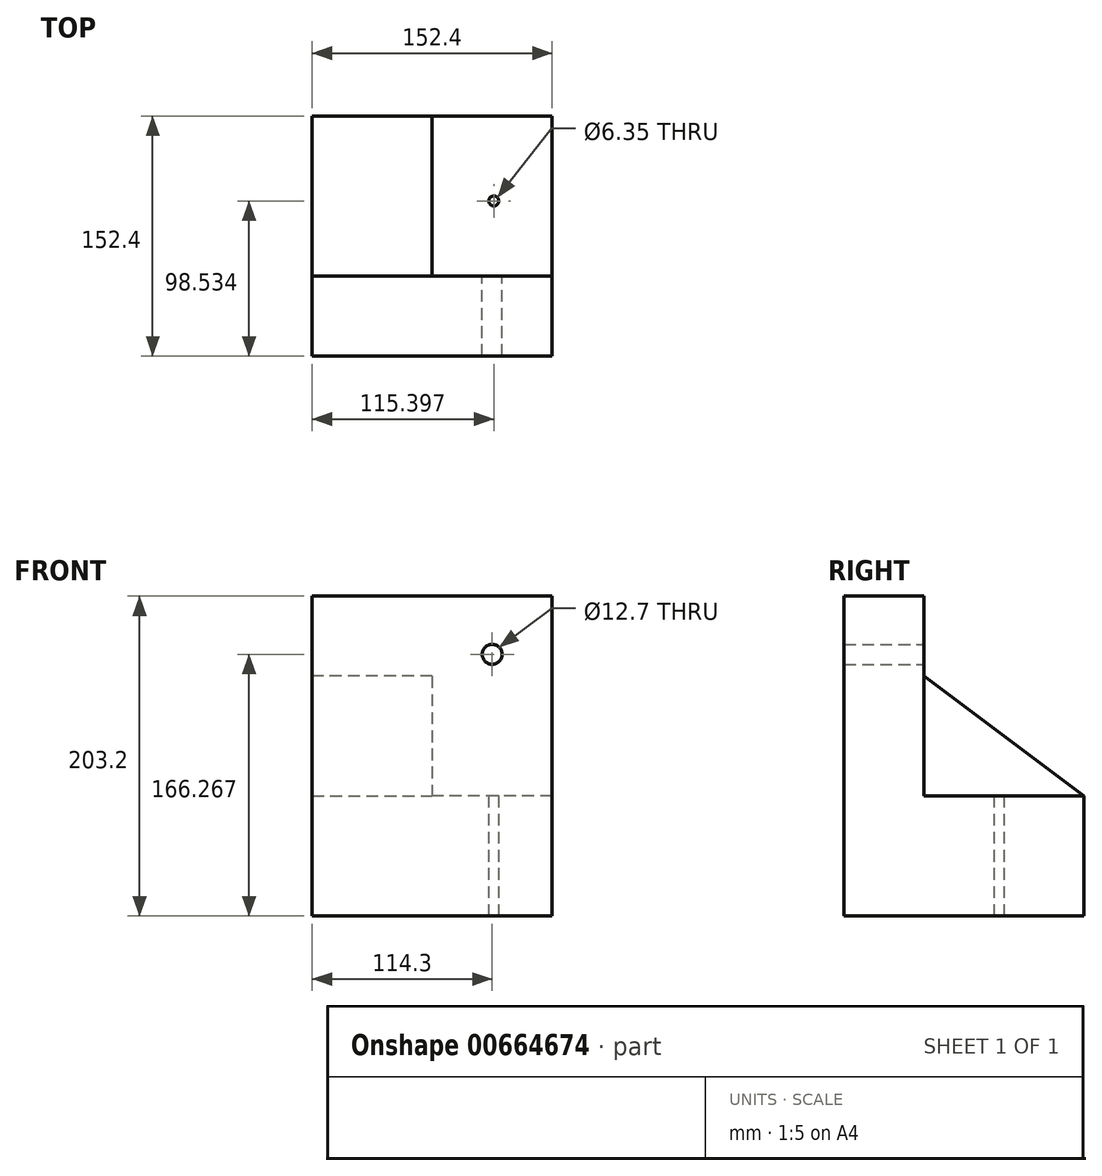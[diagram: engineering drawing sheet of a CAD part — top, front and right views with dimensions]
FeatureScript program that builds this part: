
annotation { "Feature Type Name" : "Feature", "Feature Type Description" : "" }
export const myFeature = defineFeature(function(context is Context, id is Id, definition is map)
    precondition{}
    {
        {
            var Q0;
            Q0=qCreatedBy(makeId("Right.planeOp"),FACE);
            var sketch = newSketch(context, id + "F0", { "sketchPlane" : qUnion([Q0])});
            skLineSegment(sketch, "E0", {"start": v(-50.8, 100.77) * mm, "end": v(-50.8, -102.43) * mm});
            skLineSegment(sketch, "E1", {"start": v(-50.8, -102.43) * mm, "end": v(101.6, -102.43) * mm});
            skLineSegment(sketch, "E2", {"start": v(101.6, -102.43) * mm, "end": v(101.6, -51.63) * mm});
            skLineSegment(sketch, "E3", {"start": v(101.6, -51.63) * mm, "end": v(0, -51.63) * mm});
            skLineSegment(sketch, "E4", {"start": v(0, -51.63) * mm, "end": v(0, 100.77) * mm});
            skLineSegment(sketch, "E5", {"start": v(-50.8, 100.77) * mm, "end": v(0, 100.77) * mm});
            skSolve(sketch);
        }
        {
            var Q0;
            Q0=makeQuery(id+"F0.imprint","IMPRINT",FACE,{"disambiguationData":[TD([[makeQuery(id+"F0.imprint","IMPRINT",EDGE,{"derivedFrom":sQuery(id+"F0.wireOp",EDGE,"E0")}),1.0]])]});
            extrude(context, id + "F1", {"entities" : qUnion([Q0]), "depth" : 152.4 * mm, "offsetDistance" : 25.4 * mm});
        }
        {
            var Q0;
            Q0=makeQuery(id+"F1.opExtrude","SWEPT_FACE",FACE,{"disambiguationData":[OSD([sQuery(id+"F0.wireOp",EDGE,"E3")])]});
            var sketch = newSketch(context, id + "F2", { "sketchPlane" : qUnion([Q0])});
            skLineSegment(sketch, "E6.bottom", {"start": v(50.8, 25.4) * mm, "end": v(152.4, 25.4) * mm});
            skLineSegment(sketch, "E6.top", {"start": v(50.8, 101.6) * mm, "end": v(152.4, 101.6) * mm});
            skLineSegment(sketch, "E6.left", {"start": v(50.8, 25.4) * mm, "end": v(50.8, 101.6) * mm});
            skLineSegment(sketch, "E6.right", {"start": v(152.4, 25.4) * mm, "end": v(152.4, 101.6) * mm});
            skSolve(sketch);
        }
        {
            var Q0;
            Q0 = qSketchRegion(id + "F2", true);
            var Q1;
            {var subQ5=sQuery(id+"F2.wireOp",EDGE,"E6.bottom");Q1=makeQuery(id+"F2.imprint","IMPRINT",FACE,{"disambiguationData":[TD([[makeQuery(id+"F2.imprint","IMPRINT",EDGE,{"derivedFrom":subQ5}),-1.0]])]});}
            extrude(context, id + "F3", {"entities" : qUnion([Q0, Q1]), "operationType" : NewBodyOperationType.ADD, "depth" : 25.4 * mm, "offsetDistance" : 25.4 * mm});
        }
        {
            var Q0;
            Q0=makeQuery(id+"F3.opExtrude","CAP_FACE",FACE,{"disambiguationData":[OSD([sQuery(id+"F0.wireOp",EDGE,"E2"),sQuery(id+"F0.wireOp",EDGE,"E3"),sQuery(id+"F0.wireOp",EDGE,"E4"),sQuery(id+"F2.wireOp",EDGE,"E6.top"),sQuery(id+"F2.wireOp",EDGE,"E6.right")])],"isStart":false});
            var sketch = newSketch(context, id + "F4", { "sketchPlane" : qUnion([Q0])});
            skLineSegment(sketch, "E7.bottom", {"start": v(0, 101.6) * mm, "end": v(76.2, 101.6) * mm});
            skLineSegment(sketch, "E7.top", {"start": v(0, 0) * mm, "end": v(76.2, 0) * mm});
            skLineSegment(sketch, "E7.left", {"start": v(0, 101.6) * mm, "end": v(0, 0) * mm});
            skLineSegment(sketch, "E7.right", {"start": v(76.2, 101.6) * mm, "end": v(76.2, 0) * mm});
            skSolve(sketch);
        }
        {
            var Q0;
            Q0 = qSketchRegion(id + "F4", true);
            extrude(context, id + "F5", {"entities" : qUnion([Q0]), "operationType" : NewBodyOperationType.ADD, "depth" : 76.2 * mm, "offsetDistance" : 25.4 * mm});
        }
        {
            var Q0;
            Q0=makeQuery(id+"F3.opExtrude","CAP_FACE",FACE,{"disambiguationData":[OSD([sQuery(id+"F0.wireOp",EDGE,"E2"),sQuery(id+"F0.wireOp",EDGE,"E3"),sQuery(id+"F0.wireOp",EDGE,"E4"),sQuery(id+"F2.wireOp",EDGE,"E6.top"),sQuery(id+"F2.wireOp",EDGE,"E6.right")])],"isStart":false});
            var sketch = newSketch(context, id + "F6", { "sketchPlane" : qUnion([Q0])});
            skCircle(sketch, "E8", {"center": v(115.4, 47.73) * mm, "radius": 4.76 * mm});
            skSolve(sketch);
        }
        {
            var Q0;
            Q0=sQuery(id+"F6.wireOp",VERTEX,"E8.center");
            var Q1;
            Q1=makeQuery(id+"F1.opExtrude","SWEPT_BODY",BODY,{"disambiguationData":[OSD([sQuery(id+"F0.wireOp",EDGE,"E0"),sQuery(id+"F0.wireOp",EDGE,"E1"),sQuery(id+"F0.wireOp",EDGE,"E2"),sQuery(id+"F0.wireOp",EDGE,"E3"),sQuery(id+"F0.wireOp",EDGE,"E4"),sQuery(id+"F0.wireOp",EDGE,"E5")])]});
            hole(context, id + "F7", {"style" : HoleStyle.SIMPLE, "endStyle" : HoleEndStyle.THROUGH, "holeDiameter" : 6.35 * mm, "majorDiameter" : 6.35 * mm, "isTappedThrough" : true, "tappedDepth" : 12.7 * mm, "tapClearance" : 3, "locations" : qUnion([Q0]), "scope" : qUnion([Q1])});
        }
        {
            var Q0;
            Q0=makeQuery(id+"F5.opExtrude","SWEPT_FACE",FACE,{"disambiguationData":[OSD([sQuery(id+"F4.wireOp",EDGE,"E7.right")])]});
            var sketch = newSketch(context, id + "F8", { "sketchPlane" : qUnion([Q0])});
            skLineSegment(sketch, "E9", {"start": v(0, 49.97) * mm, "end": v(101.6, -26.23) * mm});
            skLineSegment(sketch, "E10", {"start": v(101.6, -26.23) * mm, "end": v(101.6, 49.97) * mm});
            skLineSegment(sketch, "E11", {"start": v(101.6, 49.97) * mm, "end": v(0, 49.97) * mm});
            skSolve(sketch);
        }
        {
            var Q0;
            Q0 = qSketchRegion(id + "F8", true);
            extrude(context, id + "F9", {"entities" : qUnion([Q0]), "operationType" : NewBodyOperationType.REMOVE, "oppositeDirection" : true, "depth" : 76.2 * mm, "offsetDistance" : 25.4 * mm});
        }
        {
            var Q0;
            Q0=makeQuery(id+"F1.opExtrude","SWEPT_FACE",FACE,{"disambiguationData":[OSD([sQuery(id+"F0.wireOp",EDGE,"E4")])]});
            var sketch = newSketch(context, id + "F10", { "sketchPlane" : qUnion([Q0])});
            skPoint(sketch, "E12", {"position": v(-114.3, 63.84) * mm});
            skSolve(sketch);
        }
        {
            var Q0;
            Q0=sQuery(id+"F10.wireOp",VERTEX,"E12");
            var Q1;
            Q1=makeQuery(id+"F1.opExtrude","SWEPT_BODY",BODY,{"disambiguationData":[OSD([sQuery(id+"F0.wireOp",EDGE,"E0"),sQuery(id+"F0.wireOp",EDGE,"E1"),sQuery(id+"F0.wireOp",EDGE,"E2"),sQuery(id+"F0.wireOp",EDGE,"E3"),sQuery(id+"F0.wireOp",EDGE,"E4"),sQuery(id+"F0.wireOp",EDGE,"E5")])]});
            hole(context, id + "F11", {"style" : HoleStyle.SIMPLE, "endStyle" : HoleEndStyle.THROUGH, "holeDiameter" : 12.7 * mm, "majorDiameter" : 6.35 * mm, "isTappedThrough" : true, "tappedDepth" : 12.7 * mm, "tapClearance" : 3, "locations" : qUnion([Q0]), "scope" : qUnion([Q1])});
        }
    });
